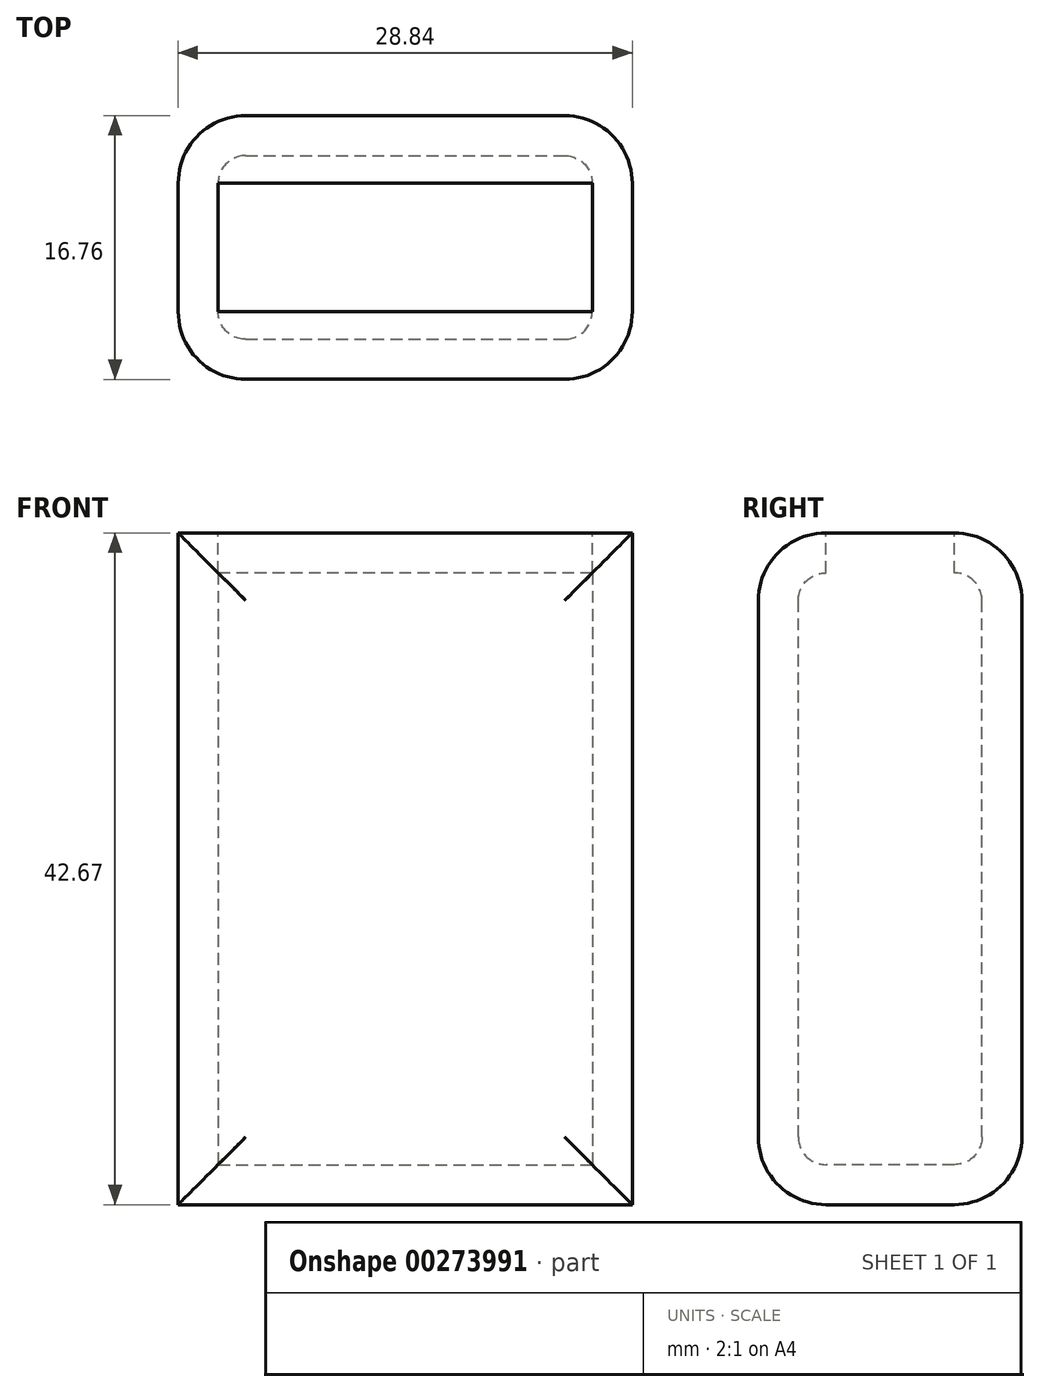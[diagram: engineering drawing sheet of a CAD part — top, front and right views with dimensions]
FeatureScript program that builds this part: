
annotation { "Feature Type Name" : "Feature", "Feature Type Description" : "" }
export const myFeature = defineFeature(function(context is Context, id is Id, definition is map)
    precondition{}
    {
        {
            var Q0;
            Q0=qCreatedBy(makeId("Top.planeOp"),FACE);
            var sketch = newSketch(context, id + "F0", { "sketchPlane" : qUnion([Q0])});
            skLineSegment(sketch, "E0.bottom", {"start": v(-14.42, 8.38) * mm, "end": v(14.42, 8.38) * mm});
            skLineSegment(sketch, "E0.top", {"start": v(-14.42, -8.38) * mm, "end": v(14.42, -8.38) * mm});
            skLineSegment(sketch, "E0.left", {"start": v(-14.42, 8.38) * mm, "end": v(-14.42, -8.38) * mm});
            skLineSegment(sketch, "E0.right", {"start": v(14.42, 8.38) * mm, "end": v(14.42, -8.38) * mm});
            skPoint(sketch, "E0.middle", {"position": v(0, 0) * mm});
            skSolve(sketch);
        }
        {
            var Q0;
            Q0=makeQuery(id+"F0.imprint","IMPRINT",FACE,{"disambiguationData":[TD([[makeQuery(id+"F0.imprint","IMPRINT",EDGE,{"derivedFrom":sQuery(id+"F0.wireOp",EDGE,"E0.bottom")}),-1.0]])]});
            extrude(context, id + "F1", {"entities" : qUnion([Q0]), "depth" : 42.67 * mm});
        }
        {
            var Q0;
            Q0=makeQuery(id+"F1.opExtrude","SWEPT_FACE",FACE,{"disambiguationData":[OSD([sQuery(id+"F0.wireOp",EDGE,"E0.top")])]});
            fillet(context, id + "F2", {"entities" : qUnion([Q0]), "radius" : 4.3 * mm, "tangentPropagation" : true, "allowEdgeOverflow" : false});
        }
        {
            var Q0;
            Q0=makeQuery(id+"F1.opExtrude","SWEPT_FACE",FACE,{"disambiguationData":[OSD([sQuery(id+"F0.wireOp",EDGE,"E0.bottom")])]});
            fillet(context, id + "F3", {"entities" : qUnion([Q0]), "radius" : 4.3 * mm, "tangentPropagation" : true, "allowEdgeOverflow" : false});
        }
        {
            var Q0;
            Q0=makeQuery(id+"F1.opExtrude","CAP_FACE",FACE,{"disambiguationData":[OSD([sQuery(id+"F0.wireOp",EDGE,"E0.bottom"),sQuery(id+"F0.wireOp",EDGE,"E0.top"),sQuery(id+"F0.wireOp",EDGE,"E0.left"),sQuery(id+"F0.wireOp",EDGE,"E0.right")])],"isStart":false});
            shell(context, id + "F4", {"entities" : qUnion([Q0]), "thickness" : 2.54 * mm});
        }
    });
